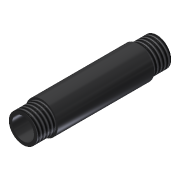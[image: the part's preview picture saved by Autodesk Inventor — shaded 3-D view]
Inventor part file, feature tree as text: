
AUTODESK INVENTOR PART (.ipt)
format: ipt  version: 2014 SP1 (Build 180222100, 222)  size: 102,912 bytes
history: native  units: in
note: dims shown in document units (in); Inventor stores cm internally (conversion verified against a paired STEP export)
features: extrude x3, sketch x3, thread x2
ambient origin geometry x8: Origin, YZ Plane, XZ Plane, XY Plane, X Axis, Y Axis, Z Axis, Center Point
bodies: Solid1 (feature_tree)
feature tree (8):
  extrude  "Extrusion1"  Depth=0.857in
  extrude  "Extrusion2"  Depth=0.5in TaperAngle=0.0deg
  thread  "Thread2"  [1 undecoded]
  extrude  "Extrusion4"  Depth=0.5in TaperAngle=0.0deg
  thread  "Thread3"  [1 undecoded]
  sketch  "Sketch1"  dims[d0=0.584in d1=0.857in]
  sketch  "Sketch2"  dims[d2=3.578in d3=0.0in d4=0.5in d5=0.0in d11=1.0in d12=0.0in]
  sketch  "Sketch4"  dims[d13=0.761in d14=0.5in d15=0.0in d16=1.0in d17=0.0in]
note: 2 required parameter values undecoded (feature->parameter linkage not recoverable at this tier; creation-order binding heuristic only, values carry confidence <= 0.55)
